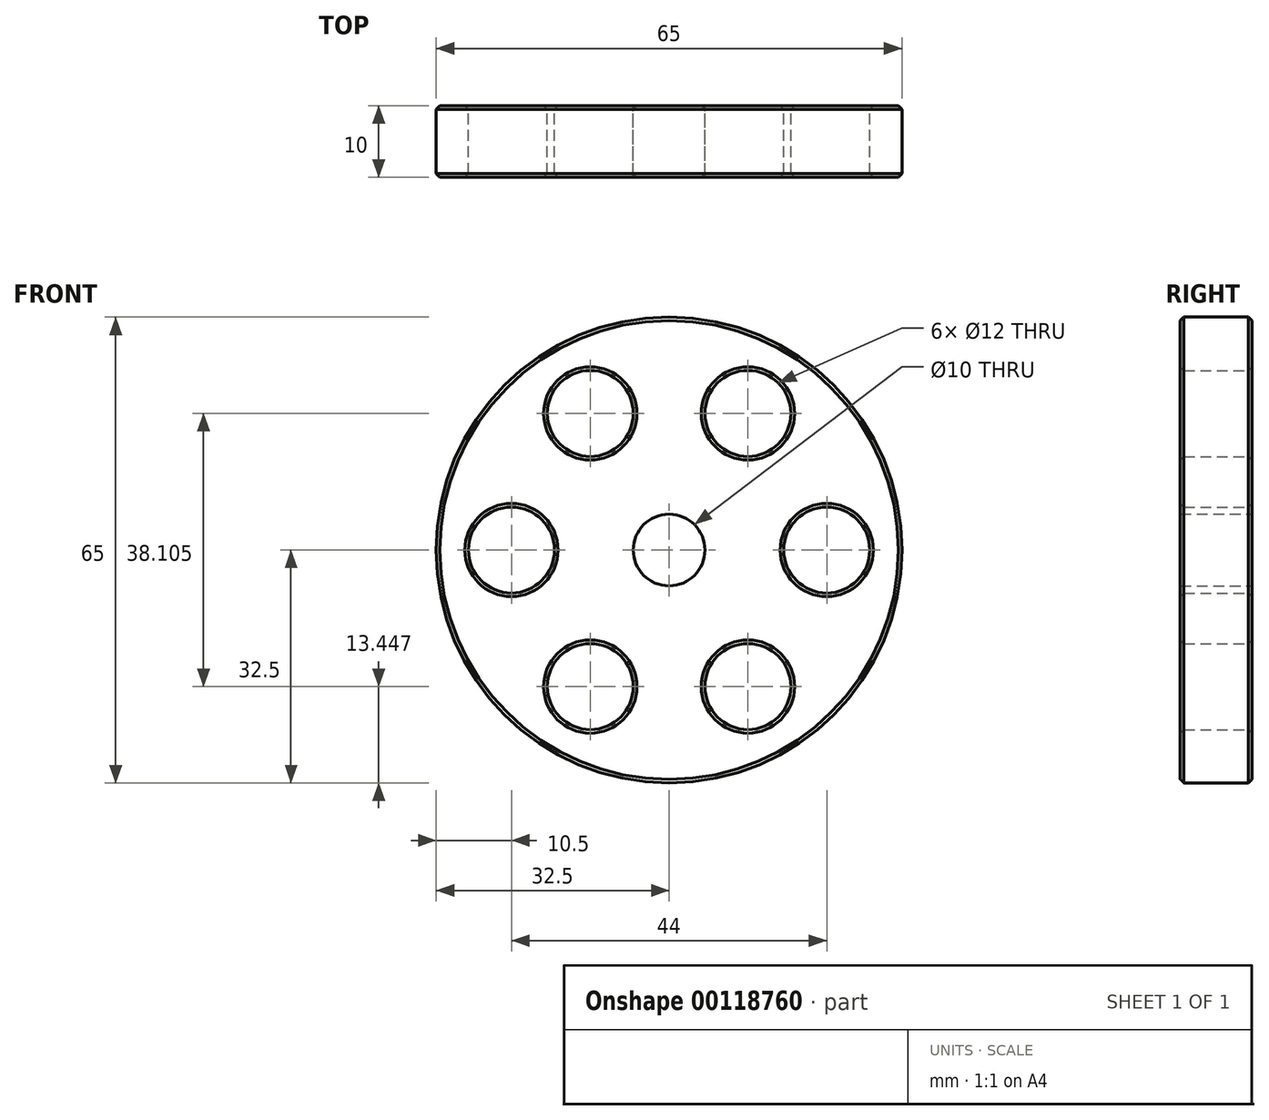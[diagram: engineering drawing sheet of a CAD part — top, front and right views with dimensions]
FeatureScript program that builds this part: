
annotation { "Feature Type Name" : "Feature", "Feature Type Description" : "" }
export const myFeature = defineFeature(function(context is Context, id is Id, definition is map)
    precondition{}
    {
        {
            var Q0;
            Q0=qCreatedBy(makeId("Front.planeOp"),FACE);
            var sketch = newSketch(context, id + "F0", { "sketchPlane" : qUnion([Q0])});
            skCircle(sketch, "E0", {"center": v(0, 0) * mm, "radius": 32.5 * mm});
            skCircle(sketch, "E1", {"center": v(0, 0) * mm, "radius": 5 * mm});
            skCircle(sketch, "E2", {"center": v(11, 19.05) * mm, "radius": 6 * mm});
            skCircle(sketch, "E3", {"center": v(22, 0) * mm, "radius": 6 * mm});
            skCircle(sketch, "E4", {"center": v(11, -19.05) * mm, "radius": 6 * mm});
            skCircle(sketch, "E5", {"center": v(-11, -19.05) * mm, "radius": 6 * mm});
            skCircle(sketch, "E6", {"center": v(-22, 0) * mm, "radius": 6 * mm});
            skCircle(sketch, "E7", {"center": v(-11, 19.05) * mm, "radius": 6 * mm});
            skSolve(sketch);
        }
        {
            var Q0;
            Q0 = qSketchRegion(id + "F0", true);
            extrude(context, id + "F1", {"entities" : qUnion([Q0]), "endBound" : BoundingType.SYMMETRIC, "depth" : 10 * mm});
        }
        {
            var Q0;
            Q0=makeQuery(id+"F1.opExtrude","CAP_EDGE",EDGE,{"disambiguationData":[OSD([sQuery(id+"F0.wireOp",EDGE,"E0")])],"isStart":false});
            chamfer(context, id + "F2", {"entities" : qUnion([Q0]), "width" : 0.5 * mm, "tangentPropagation" : true});
        }
        {
            var Q0;
            Q0=makeQuery(id+"F1.opExtrude","CAP_EDGE",EDGE,{"disambiguationData":[OSD([sQuery(id+"F0.wireOp",EDGE,"E4")])],"isStart":true});
            var Q1;
            Q1=makeQuery(id+"F1.opExtrude","CAP_EDGE",EDGE,{"disambiguationData":[OSD([sQuery(id+"F0.wireOp",EDGE,"E4")])],"isStart":false});
            var Q2;
            Q2=makeQuery(id+"F1.opExtrude","CAP_EDGE",EDGE,{"disambiguationData":[OSD([sQuery(id+"F0.wireOp",EDGE,"E3")])],"isStart":true});
            var Q3;
            Q3=makeQuery(id+"F1.opExtrude","CAP_EDGE",EDGE,{"disambiguationData":[OSD([sQuery(id+"F0.wireOp",EDGE,"E2")])],"isStart":true});
            var Q4;
            Q4=makeQuery(id+"F1.opExtrude","CAP_EDGE",EDGE,{"disambiguationData":[OSD([sQuery(id+"F0.wireOp",EDGE,"E0")])],"isStart":true});
            var Q5;
            Q5=makeQuery(id+"F1.opExtrude","CAP_EDGE",EDGE,{"disambiguationData":[OSD([sQuery(id+"F0.wireOp",EDGE,"E7")])],"isStart":true});
            var Q6;
            Q6=makeQuery(id+"F1.opExtrude","CAP_EDGE",EDGE,{"disambiguationData":[OSD([sQuery(id+"F0.wireOp",EDGE,"E6")])],"isStart":true});
            var Q7;
            Q7=makeQuery(id+"F1.opExtrude","CAP_EDGE",EDGE,{"disambiguationData":[OSD([sQuery(id+"F0.wireOp",EDGE,"E5")])],"isStart":true});
            var Q8;
            Q8=makeQuery(id+"F1.opExtrude","CAP_EDGE",EDGE,{"disambiguationData":[OSD([sQuery(id+"F0.wireOp",EDGE,"E3")])],"isStart":false});
            var Q9;
            Q9=makeQuery(id+"F1.opExtrude","CAP_EDGE",EDGE,{"disambiguationData":[OSD([sQuery(id+"F0.wireOp",EDGE,"E2")])],"isStart":false});
            var Q10;
            Q10=makeQuery(id+"F1.opExtrude","CAP_EDGE",EDGE,{"disambiguationData":[OSD([sQuery(id+"F0.wireOp",EDGE,"E7")])],"isStart":false});
            var Q11;
            Q11=makeQuery(id+"F1.opExtrude","CAP_EDGE",EDGE,{"disambiguationData":[OSD([sQuery(id+"F0.wireOp",EDGE,"E5")])],"isStart":false});
            chamfer(context, id + "F3", {"entities" : qUnion([Q0, Q1, Q2, Q3, Q4, Q5, Q6, Q7, Q8, Q9, Q10, Q11]), "width" : 0.5 * mm});
        }
        {
            var Q0;
            Q0=makeQuery(id+"F1.opExtrude","CAP_EDGE",EDGE,{"disambiguationData":[OSD([sQuery(id+"F0.wireOp",EDGE,"E6")])],"isStart":false});
            chamfer(context, id + "F4", {"entities" : qUnion([Q0]), "width" : 0.5 * mm, "tangentPropagation" : true});
        }
    });
